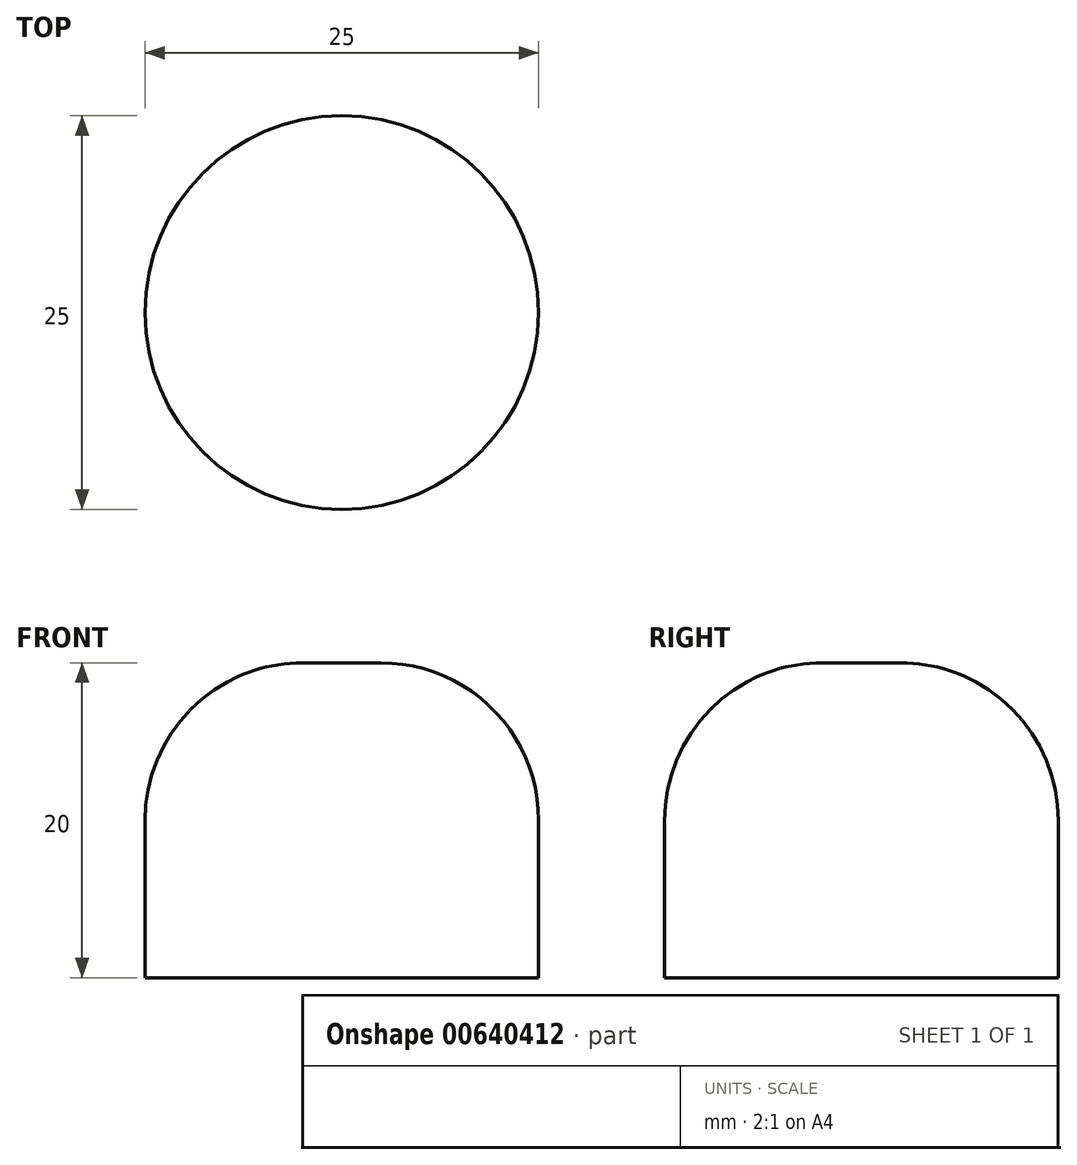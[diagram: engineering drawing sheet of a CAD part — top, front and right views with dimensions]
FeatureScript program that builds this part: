
annotation { "Feature Type Name" : "Feature", "Feature Type Description" : "" }
export const myFeature = defineFeature(function(context is Context, id is Id, definition is map)
    precondition{}
    {
        {
            var Q0;
            Q0=qCreatedBy(makeId("Top.planeOp"),FACE);
            var sketch = newSketch(context, id + "F0", { "sketchPlane" : qUnion([Q0])});
            skCircle(sketch, "E0", {"center": v(0, 0) * mm, "radius": 12.5 * mm});
            skSolve(sketch);
        }
        {
            var Q0;
            Q0 = qSketchRegion(id + "F0", true);
            extrude(context, id + "F1", {"entities" : qUnion([Q0]), "depth" : 20 * mm, "offsetDistance" : 25 * mm});
        }
        {
            var Q0;
            Q0=makeQuery(id+"F1.opExtrude","CAP_FACE",FACE,{"disambiguationData":[OSD([sQuery(id+"F0.wireOp",EDGE,"E0")])],"isStart":false});
            fillet(context, id + "F2", {"entities" : qUnion([Q0]), "radius" : 10 * mm, "tangentPropagation" : true, "allowEdgeOverflow" : false});
        }
    });
